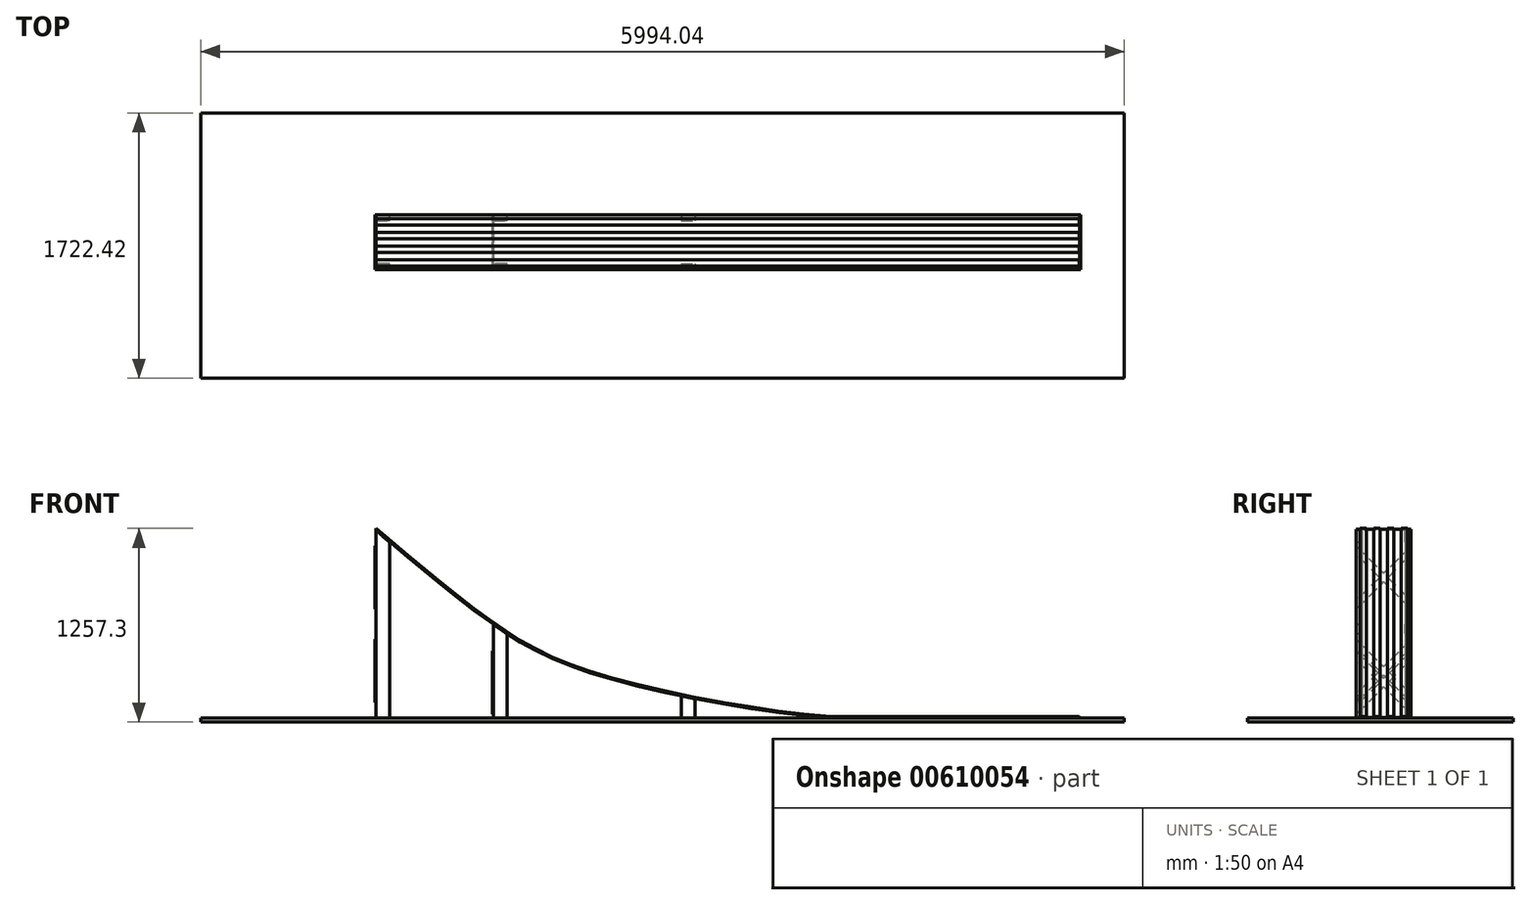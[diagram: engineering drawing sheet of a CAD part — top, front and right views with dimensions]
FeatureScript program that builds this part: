
annotation { "Feature Type Name" : "Feature", "Feature Type Description" : "" }
export const myFeature = defineFeature(function(context is Context, id is Id, definition is map)
    precondition{}
    {
        {
            var Q0;
            Q0=qCreatedBy(makeId("Front.planeOp"),FACE);
            var sketch = newSketch(context, id + "F0", { "sketchPlane" : qUnion([Q0])});
            skFitSpline(sketch, "E0", {"points": [v(0, 0) * mm, v(762, -609.6) * mm, v(1524, -965.2) * mm, v(3048, -1219.2) * mm], "startDerivative": vector(2305.98, -1939.89) * mm, "endDerivative": vector(2427.56, 0) * mm});
            skLineSegment(sketch, "E1", {"start": v(3048, -1219.2) * mm, "end": v(4572, -1219.2) * mm});
            skSolve(sketch);
        }
        {
            var Q0;
            Q0=qCreatedBy(makeId("Right.planeOp"),FACE);
            var sketch = newSketch(context, id + "F1", { "sketchPlane" : qUnion([Q0])});
            skLineSegment(sketch, "E2.bottom", {"start": v(177.8, 0) * mm, "end": v(-177.8, 0) * mm});
            skLineSegment(sketch, "E2.top", {"start": v(177.8, 6.35) * mm, "end": v(153.99, 6.35) * mm});
            skLineSegment(sketch, "E2.left", {"start": v(177.8, 0) * mm, "end": v(177.8, 6.35) * mm});
            skLineSegment(sketch, "E2.right", {"start": v(-177.8, 0) * mm, "end": v(-177.8, 6.35) * mm});
            skLineSegment(sketch, "E3.bottom", {"start": v(-153.99, 12.7) * mm, "end": v(-112.71, 12.7) * mm});
            skLineSegment(sketch, "E3.left", {"start": v(-153.99, 12.7) * mm, "end": v(-153.99, 6.35) * mm});
            skLineSegment(sketch, "E3.right", {"start": v(-112.71, 12.7) * mm, "end": v(-112.71, 6.35) * mm});
            skLineSegment(sketch, "E4.trimOffspring", {"start": v(-153.99, 6.35) * mm, "end": v(-177.8, 6.35) * mm});
            skLineSegment(sketch, "E5.bottom", {"start": v(-65.09, 12.7) * mm, "end": v(-23.81, 12.7) * mm});
            skLineSegment(sketch, "E5.left", {"start": v(-65.09, 12.7) * mm, "end": v(-65.09, 6.35) * mm});
            skLineSegment(sketch, "E5.right", {"start": v(-23.81, 12.7) * mm, "end": v(-23.81, 6.35) * mm});
            skLineSegment(sketch, "E6.trimOffspring", {"start": v(-65.09, 6.35) * mm, "end": v(-112.71, 6.35) * mm});
            skLineSegment(sketch, "E7.MirrorCS", {"start": v(153.99, 12.7) * mm, "end": v(153.99, 6.35) * mm});
            skLineSegment(sketch, "E8.MirrorCS", {"start": v(153.99, 12.7) * mm, "end": v(112.71, 12.7) * mm});
            skLineSegment(sketch, "E9.MirrorCS", {"start": v(65.09, 6.35) * mm, "end": v(112.71, 6.35) * mm});
            skLineSegment(sketch, "E10.MirrorCS", {"start": v(112.71, 12.7) * mm, "end": v(112.71, 6.35) * mm});
            skLineSegment(sketch, "E11.MirrorCS", {"start": v(153.99, 6.35) * mm, "end": v(177.8, 6.35) * mm});
            skLineSegment(sketch, "E12.MirrorCS", {"start": v(23.81, 12.7) * mm, "end": v(23.81, 6.35) * mm});
            skLineSegment(sketch, "E13.MirrorCS", {"start": v(65.09, 12.7) * mm, "end": v(23.81, 12.7) * mm});
            skLineSegment(sketch, "E14.MirrorCS", {"start": v(65.09, 12.7) * mm, "end": v(65.09, 6.35) * mm});
            skLineSegment(sketch, "E15.trimOffspring", {"start": v(23.81, 6.35) * mm, "end": v(-23.81, 6.35) * mm});
            skLineSegment(sketch, "E16.trimOffspring", {"start": v(112.71, 6.35) * mm, "end": v(65.09, 6.35) * mm});
            skSolve(sketch);
        }
        {
            var Q0;
            Q0=makeQuery(id+"F1.imprint","IMPRINT",FACE,{"disambiguationData":[TD([[makeQuery(id+"F1.imprint","IMPRINT",EDGE,{"derivedFrom":sQuery(id+"F1.wireOp",EDGE,"E2.bottom")}),-1.0]])]});
            var Q1;
            Q1 = qConstructionFilter(qBodyType(qCreatedBy(id + "F0" ,EDGE), BodyType.WIRE), ConstructionObject.NO);
            sweep(context, id + "F2", {"profiles" : qUnion([Q0]), "path" : qUnion([Q1])});
        }
        {
            var Q0;
            Q0=qCreatedBy(makeId("Top.planeOp"),FACE);
            cPlane(context, id + "F3", {"entities" : qUnion([Q0]), "cplaneType" : CPlaneType.OFFSET, "offset" : 1219.2 * mm, "oppositeDirection" : true, "width" : 152.4 * mm, "height" : 152.4 * mm});
        }
        {
            var Q0;
            Q0=qCreatedBy(id+"F3.planeOp",FACE);
            var sketch = newSketch(context, id + "F4", { "sketchPlane" : qUnion([Q0])});
            skLineSegment(sketch, "E17.bottom", {"start": v(-1136.8, 840.01) * mm, "end": v(4857.24, 840.01) * mm});
            skLineSegment(sketch, "E17.top", {"start": v(-1136.8, -882.41) * mm, "end": v(4857.24, -882.41) * mm});
            skLineSegment(sketch, "E17.left", {"start": v(-1136.8, 840.01) * mm, "end": v(-1136.8, -882.41) * mm});
            skLineSegment(sketch, "E17.right", {"start": v(4857.24, 840.01) * mm, "end": v(4857.24, -882.41) * mm});
            skSolve(sketch);
        }
        {
            var Q0;
            Q0=makeQuery(id+"F4.imprint","IMPRINT",FACE,{"disambiguationData":[TD([[makeQuery(id+"F4.imprint","IMPRINT",EDGE,{"derivedFrom":sQuery(id+"F4.wireOp",EDGE,"E17.bottom")}),-1.0]])]});
            var Q1;
            Q1=sQuery(id+"F4.wireOp",EDGE,"E17.top");
            extrude(context, id + "F5", {"entities" : qUnion([Q0]), "surfaceEntities" : qUnion([Q1]), "oppositeDirection" : true, "depth" : 25.4 * mm, "offsetDistance" : 25.4 * mm});
        }
        {
            var Q0;
            Q0=qCreatedBy(id+"F3.planeOp",FACE);
            var sketch = newSketch(context, id + "F6", { "sketchPlane" : qUnion([Q0])});
            skLineSegment(sketch, "E18.bottom", {"start": v(0, 177.8) * mm, "end": v(88.9, 177.8) * mm});
            skLineSegment(sketch, "E18.top", {"start": v(0, 139.7) * mm, "end": v(88.9, 139.7) * mm});
            skLineSegment(sketch, "E18.left", {"start": v(0, 177.8) * mm, "end": v(0, 139.7) * mm});
            skLineSegment(sketch, "E18.right", {"start": v(88.9, 177.8) * mm, "end": v(88.9, 139.7) * mm});
            skLineSegment(sketch, "E19.bottom", {"start": v(762, 177.8) * mm, "end": v(850.9, 177.8) * mm});
            skLineSegment(sketch, "E19.top", {"start": v(762, 139.7) * mm, "end": v(850.9, 139.7) * mm});
            skLineSegment(sketch, "E19.left", {"start": v(762, 177.8) * mm, "end": v(762, 139.7) * mm});
            skLineSegment(sketch, "E19.right", {"start": v(850.9, 177.8) * mm, "end": v(850.9, 139.7) * mm});
            skLineSegment(sketch, "E20.bottom", {"start": v(1981.2, 177.8) * mm, "end": v(2070.1, 177.8) * mm});
            skLineSegment(sketch, "E20.top", {"start": v(1981.2, 139.7) * mm, "end": v(2070.1, 139.7) * mm});
            skLineSegment(sketch, "E20.left", {"start": v(1981.2, 177.8) * mm, "end": v(1981.2, 139.7) * mm});
            skLineSegment(sketch, "E20.right", {"start": v(2070.1, 177.8) * mm, "end": v(2070.1, 139.7) * mm});
            skLineSegment(sketch, "E21.MirrorCS", {"start": v(88.9, -177.8) * mm, "end": v(88.9, -139.7) * mm});
            skLineSegment(sketch, "E22.MirrorCS", {"start": v(0, -139.7) * mm, "end": v(88.9, -139.7) * mm});
            skLineSegment(sketch, "E23.MirrorCS", {"start": v(0, -177.8) * mm, "end": v(0, -139.7) * mm});
            skLineSegment(sketch, "E24.MirrorCS", {"start": v(762, -177.8) * mm, "end": v(850.9, -177.8) * mm});
            skLineSegment(sketch, "E25.MirrorCS", {"start": v(762, -139.7) * mm, "end": v(850.9, -139.7) * mm});
            skLineSegment(sketch, "E26.MirrorCS", {"start": v(0, -177.8) * mm, "end": v(88.9, -177.8) * mm});
            skLineSegment(sketch, "E27.MirrorCS", {"start": v(2070.1, -177.8) * mm, "end": v(2070.1, -139.7) * mm});
            skLineSegment(sketch, "E28.MirrorCS", {"start": v(1981.2, -177.8) * mm, "end": v(1981.2, -139.7) * mm});
            skLineSegment(sketch, "E29.MirrorCS", {"start": v(1981.2, -139.7) * mm, "end": v(2070.1, -139.7) * mm});
            skLineSegment(sketch, "E30.MirrorCS", {"start": v(762, -177.8) * mm, "end": v(762, -139.7) * mm});
            skLineSegment(sketch, "E31.MirrorCS", {"start": v(1981.2, -177.8) * mm, "end": v(2070.1, -177.8) * mm});
            skLineSegment(sketch, "E32.MirrorCS", {"start": v(850.9, -177.8) * mm, "end": v(850.9, -139.7) * mm});
            skSolve(sketch);
        }
        {
            var Q0;
            Q0 = qSketchRegion(id + "F6", true);
            var Q1;
            Q1=makeQuery(id+"F2.opSweep","SWEPT_FACE",FACE,{"disambiguationData":[OSD([sQuery(id+"F0.wireOp",EDGE,"E0"),sQuery(id+"F1.wireOp",EDGE,"E2.bottom")])]});
            extrude(context, id + "F7", {"entities" : qUnion([Q0]), "endBound" : BoundingType.UP_TO_SURFACE, "depth" : 25.4 * mm, "endBoundEntityFace" : qUnion([Q1]), "offsetDistance" : 25.4 * mm});
        }
        {
            var Q0;
            Q0=qCreatedBy(makeId("Right.planeOp"),FACE);
            var sketch = newSketch(context, id + "F8", { "sketchPlane" : qUnion([Q0])});
            skLineSegment(sketch, "E33", {"start": v(177.8, -101.6) * mm, "end": v(0, -279.4) * mm});
            skLineSegment(sketch, "E34", {"start": v(-177.8, -511.08) * mm, "end": v(-177.8, -457.2) * mm});
            skLineSegment(sketch, "E35", {"start": v(-177.8, -511.08) * mm, "end": v(0, -333.28) * mm});
            skLineSegment(sketch, "E36", {"start": v(177.8, -101.6) * mm, "end": v(177.8, -155.48) * mm});
            skLineSegment(sketch, "E37", {"start": v(-177.8, -511.08) * mm, "end": v(-204.74, -484.14) * mm, "construction": true});
            skLineSegment(sketch, "E38", {"start": v(-204.74, -484.14) * mm, "end": v(-177.8, -457.2) * mm, "construction": true});
            skLineSegment(sketch, "E39", {"start": v(177.8, -155.48) * mm, "end": v(204.74, -128.54) * mm, "construction": true});
            skLineSegment(sketch, "E40", {"start": v(204.74, -128.54) * mm, "end": v(177.8, -101.6) * mm, "construction": true});
            skLineSegment(sketch, "E41", {"start": v(130.23, -609.6) * mm, "end": v(-102.74, -609.6) * mm, "construction": true});
            skLineSegment(sketch, "E42.MirrorCS", {"start": v(177.8, -511.08) * mm, "end": v(177.8, -457.2) * mm});
            skLineSegment(sketch, "E43.MirrorCS", {"start": v(-177.8, -101.6) * mm, "end": v(-177.8, -155.48) * mm});
            skLineSegment(sketch, "E44.MirrorCS", {"start": v(177.8, -511.08) * mm, "end": v(0, -333.28) * mm});
            skLineSegment(sketch, "E45.MirrorCS", {"start": v(-177.8, -101.6) * mm, "end": v(0, -279.4) * mm});
            skLineSegment(sketch, "E46.trimOffspring", {"start": v(26.94, -306.34) * mm, "end": v(177.8, -155.48) * mm});
            skLineSegment(sketch, "E47.trimOffspring", {"start": v(26.94, -306.34) * mm, "end": v(177.8, -457.2) * mm});
            skLineSegment(sketch, "E48.trimOffspring", {"start": v(-26.94, -306.34) * mm, "end": v(-177.8, -457.2) * mm});
            skLineSegment(sketch, "E49.trimOffspring", {"start": v(-26.94, -306.34) * mm, "end": v(-177.8, -155.48) * mm});
            skLineSegment(sketch, "E50.MirrorCS", {"start": v(-204.74, -735.06) * mm, "end": v(-177.8, -762) * mm, "construction": true});
            skLineSegment(sketch, "E51.MirrorCS", {"start": v(177.8, -1063.72) * mm, "end": v(204.74, -1090.66) * mm, "construction": true});
            skLineSegment(sketch, "E52.MirrorCS", {"start": v(-177.8, -708.12) * mm, "end": v(-204.74, -735.06) * mm, "construction": true});
            skLineSegment(sketch, "E53.MirrorCS", {"start": v(204.74, -1090.66) * mm, "end": v(177.8, -1117.6) * mm, "construction": true});
            skLineSegment(sketch, "E54.MirrorCS", {"start": v(26.94, -912.86) * mm, "end": v(177.8, -1063.72) * mm});
            skLineSegment(sketch, "E55.MirrorCS", {"start": v(26.94, -912.86) * mm, "end": v(177.8, -762) * mm});
            skLineSegment(sketch, "E56.MirrorCS", {"start": v(-26.94, -912.86) * mm, "end": v(-177.8, -762) * mm});
            skLineSegment(sketch, "E57.MirrorCS", {"start": v(177.8, -1117.6) * mm, "end": v(0, -939.8) * mm});
            skLineSegment(sketch, "E58.MirrorCS", {"start": v(-177.8, -708.12) * mm, "end": v(0, -885.92) * mm});
            skLineSegment(sketch, "E59.MirrorCS", {"start": v(177.8, -708.12) * mm, "end": v(177.8, -762) * mm});
            skLineSegment(sketch, "E60.MirrorCS", {"start": v(-26.94, -912.86) * mm, "end": v(-177.8, -1063.72) * mm});
            skLineSegment(sketch, "E61.MirrorCS", {"start": v(-177.8, -1117.6) * mm, "end": v(-177.8, -1063.72) * mm});
            skLineSegment(sketch, "E62.MirrorCS", {"start": v(-177.8, -708.12) * mm, "end": v(-177.8, -762) * mm});
            skLineSegment(sketch, "E63.MirrorCS", {"start": v(177.8, -1117.6) * mm, "end": v(177.8, -1063.72) * mm});
            skLineSegment(sketch, "E64.MirrorCS", {"start": v(177.8, -708.12) * mm, "end": v(0, -885.92) * mm});
            skLineSegment(sketch, "E65.MirrorCS", {"start": v(-177.8, -1117.6) * mm, "end": v(0, -939.8) * mm});
            skSolve(sketch);
        }
        {
            var Q0;
            Q0 = qSketchRegion(id + "F8", true);
            extrude(context, id + "F9", {"entities" : qUnion([Q0]), "oppositeDirection" : true, "depth" : 6.35 * mm, "offsetDistance" : 25.4 * mm});
        }
        {
            var Q0;
            Q0=makeQuery(id+"F7.opExtrude","SWEPT_FACE",FACE,{"disambiguationData":[OSD([sQuery(id+"F6.wireOp",EDGE,"E19.left")])]});
            var sketch = newSketch(context, id + "F10", { "sketchPlane" : qUnion([Q0])});
            skLineSegment(sketch, "E66", {"start": v(177.8, -784.32) * mm, "end": v(0, -962.12) * mm});
            skLineSegment(sketch, "E67", {"start": v(-177.8, -1193.8) * mm, "end": v(-177.8, -1139.92) * mm});
            skLineSegment(sketch, "E68", {"start": v(-177.8, -1193.8) * mm, "end": v(0, -1016) * mm});
            skLineSegment(sketch, "E69", {"start": v(177.8, -784.32) * mm, "end": v(177.8, -838.2) * mm});
            skLineSegment(sketch, "E70", {"start": v(-177.8, -1193.8) * mm, "end": v(-204.74, -1166.86) * mm, "construction": true});
            skLineSegment(sketch, "E71", {"start": v(-204.74, -1166.86) * mm, "end": v(-177.8, -1139.92) * mm, "construction": true});
            skLineSegment(sketch, "E72", {"start": v(177.8, -838.2) * mm, "end": v(204.74, -811.26) * mm, "construction": true});
            skLineSegment(sketch, "E73", {"start": v(204.74, -811.26) * mm, "end": v(177.8, -784.32) * mm, "construction": true});
            skLineSegment(sketch, "E74.MirrorCS", {"start": v(177.8, -1193.8) * mm, "end": v(177.8, -1139.92) * mm});
            skLineSegment(sketch, "E75.MirrorCS", {"start": v(-177.8, -784.32) * mm, "end": v(-177.8, -838.2) * mm});
            skLineSegment(sketch, "E76.MirrorCS", {"start": v(177.8, -1193.8) * mm, "end": v(0, -1016) * mm});
            skLineSegment(sketch, "E77.MirrorCS", {"start": v(-177.8, -784.32) * mm, "end": v(0, -962.12) * mm});
            skLineSegment(sketch, "E78.trimOffspring", {"start": v(26.94, -989.06) * mm, "end": v(177.8, -838.2) * mm});
            skLineSegment(sketch, "E79.trimOffspring", {"start": v(26.94, -989.06) * mm, "end": v(177.8, -1139.92) * mm});
            skLineSegment(sketch, "E80.trimOffspring", {"start": v(-26.94, -989.06) * mm, "end": v(-177.8, -1139.92) * mm});
            skLineSegment(sketch, "E81.trimOffspring", {"start": v(-26.94, -989.06) * mm, "end": v(-177.8, -838.2) * mm});
            skSolve(sketch);
        }
        {
            var Q0;
            Q0 = qSketchRegion(id + "F10", true);
            extrude(context, id + "F11", {"entities" : qUnion([Q0]), "depth" : 6.35 * mm, "offsetDistance" : 25.4 * mm});
        }
    });
